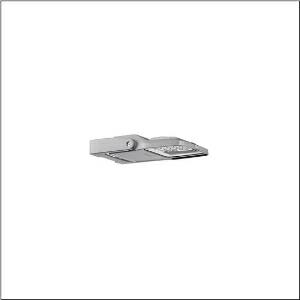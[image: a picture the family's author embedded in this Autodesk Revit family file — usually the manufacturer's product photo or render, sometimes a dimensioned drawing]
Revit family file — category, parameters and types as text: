
# Revit family: floodlight_fl_21_micro___pl43_5xa7761a4a2a_769c
name_source: partatom
category: Lighting Fixtures
units: mm (PartAtom-declared; Revit-internal decimal feet)

## family parameters
Cut with Voids When Loaded = No
Host = Face
Light Source = No
Part Type = Normal
Room Calculation Point = No
Round Connector Dimension = Use Diameter
Shared = No

## types (1)
- --- (1 x LED, 3170 lm, 23.1 W, 4000K)
    Apparent Load = 23 VA
    CIE Flux Codes = 29 80 99 100 100
    Color Rendering = 70
    Color Temperature = 4000K
    Default Elevation = 1800 mm
    Description = Floodlight FL 21 micro, floodlight, primary light control with lens, of PMMA, primary optical cover: protective disc, of toughened safety glass, transparent, light distribution: PL43, light emission: direct distribution, installation type: surface-mounted, LED, High Power LED, rated luminous flux: 3.170lm, luminous efficacy: 137lm/W, light colour: 740, colour temperature: 4000K, control gear: ECG iQ, control: optimised constant luminous flux control (CLO 2.0), Desk-Remote (wireless, voltage-free reading and setting of iQ features in the workshop via application-optimized NFC function/RFID function), Light-Fading, Smart-Wire, Night-Set, Lumen-Switch, Temp-Guard, Auto-Match, with terminal, 6-pole, mains connection: 220..240V, AC, 50/60Hz, start of lifetime: 23W, end of lifetime: 24W, reduction: 11W, luminaire housing, of diecast aluminium, powder-coated, Siteco® metallic grey (DB 702S), corrosivity category C5 according to DIN EN ISO 12944, design bracket, of diecast aluminium, powder-coated, Siteco® metallic grey (DB 702S), protection rating (complete): IP66, insulation class (complete): insulation class II (safety insulation), certification: CE, protection symbol: D, impact resistance: IK07, permissible operating ambient temperature: -40..+40°C, permissible operating ambient temperature for outdoor applications: -40..+50°C, standard: DIN EN 12944, packaging unit: 1 piece

Light Distribution: PL43
    Height = 65 mm
    Lamp = 1 x LED
    Lamp Light Flux = 3170 lm
    Lamp Power = 23.1 W
    Lamp count = 1
    Length = 312 mm
    Luminous efficacy = 137 lm/W
    Manufacturer = Siteco
    ModVariant = No
    Model = 5XA7761A4A2A
    Number of Poles = 1
    OnlyDefault = Yes
    Power Factor = 1
    Product Name = Floodlight FL 21 micro | PL43
    Product group = floodlight | pylon top
    ProductGroupID = 6101
    Protection Class = Protection class II
    Protection Degree = IP 66
    RLX_Detail_Level = 1
    RlxData = <blob elided: 97397 chars, md5=38fbd263>
    Socket = socket
    Standby Power = 0 W
    System Light Flux = 3170 lm
    System Power = 23 W
    Type Comments = factory setting: luminous flux: 100 % | dim-lin: 254 | 455 mA
    Type Image = l_1006878.jpg
    URL = http://relux.com
    VarID = @adj_090037
    Voltage = 0 V
    Weight = 0.00 kg
    Width = 230 mm

## geometry (parser evidence)
native form markers: Blend x4, Sweep x14
no freeform markers — native parametric forms only
